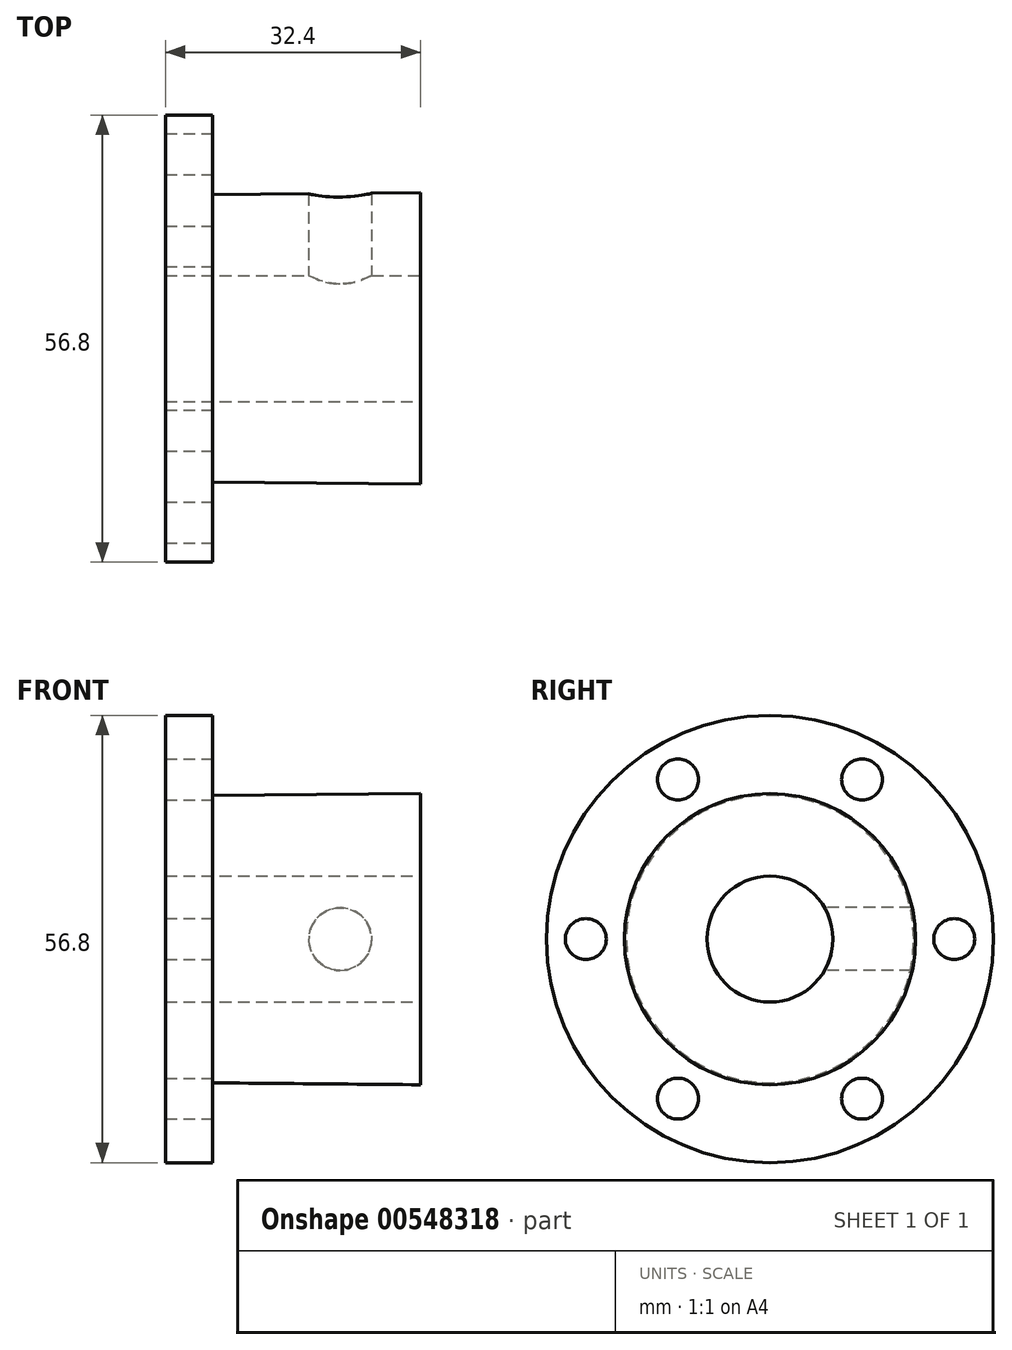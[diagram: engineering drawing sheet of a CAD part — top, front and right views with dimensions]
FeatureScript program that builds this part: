
annotation { "Feature Type Name" : "Feature", "Feature Type Description" : "" }
export const myFeature = defineFeature(function(context is Context, id is Id, definition is map)
    precondition{}
    {
        {
            var Q0;
            Q0=qCreatedBy(makeId("Front.planeOp"),FACE);
            var sketch = newSketch(context, id + "F0", { "sketchPlane" : qUnion([Q0])});
            skLineSegment(sketch, "E0", {"start": v(44.45, 0) * mm, "end": v(0, 0) * mm});
            skLineSegment(sketch, "E1", {"start": v(48.08, 18.5) * mm, "end": v(48.08, 8) * mm});
            skLineSegment(sketch, "E2", {"start": v(48.08, 8) * mm, "end": v(15.68, 8) * mm});
            skLineSegment(sketch, "E3", {"start": v(15.68, 8) * mm, "end": v(15.68, 28.4) * mm});
            skLineSegment(sketch, "E4", {"start": v(15.68, 28.4) * mm, "end": v(21.68, 28.4) * mm});
            skLineSegment(sketch, "E5", {"start": v(21.68, 28.4) * mm, "end": v(21.68, 18.26) * mm});
            skLineSegment(sketch, "E6", {"start": v(21.68, 18.26) * mm, "end": v(48.08, 18.5) * mm});
            skSolve(sketch);
        }
        {
            var Q0;
            Q0=qSketchRegion(id+"F0",true);
            var Q1;
            Q1=sQuery(id+"F0.wireOp",EDGE,"E0");
            revolve(context, id + "F1", {"entities" : qUnion([Q0]), "axis" : qUnion([Q1]), "revolveType" : RevolveType.FULL});
        }
        {
            var Q0;
            Q0=makeQuery(id+"F1.opRevolve","SWEPT_FACE",FACE,{"disambiguationData":[OSD([sQuery(id+"F0.wireOp",EDGE,"E5")])]});
            var sketch = newSketch(context, id + "F2", { "sketchPlane" : qUnion([Q0])});
            skLineSegment(sketch, "E7", {"start": v(0, 0) * mm, "end": v(-46.8, 0) * mm, "construction": true});
            skCircle(sketch, "E8", {"center": v(-23.4, 0) * mm, "radius": 2.6 * mm});
            skCircle(sketch, "E9.1.0", {"center": v(-11.7, -20.26) * mm, "radius": 2.6 * mm});
            skCircle(sketch, "E9.2.0", {"center": v(11.7, -20.26) * mm, "radius": 2.6 * mm});
            skCircle(sketch, "E9.3.0", {"center": v(23.4, 0) * mm, "radius": 2.6 * mm});
            skCircle(sketch, "E9.4.0", {"center": v(11.7, 20.26) * mm, "radius": 2.6 * mm});
            skCircle(sketch, "E9.5.0", {"center": v(-11.7, 20.26) * mm, "radius": 2.6 * mm});
            skPoint(sketch, "E9.center", {"position": v(0, 0) * mm});
            skSolve(sketch);
        }
        {
            var Q0;
            Q0=qSketchRegion(id+"F2",true);
            extrude(context, id + "F3", {"entities" : qUnion([Q0]), "operationType" : NewBodyOperationType.REMOVE, "oppositeDirection" : true, "depth" : 6 * mm, "offsetDistance" : 25 * mm});
        }
        {
            var Q0;
            Q0=qCreatedBy(makeId("Front.planeOp"),FACE);
            var sketch = newSketch(context, id + "F4", { "sketchPlane" : qUnion([Q0])});
            skCircle(sketch, "E10", {"center": v(37.88, 0) * mm, "radius": 4 * mm});
            skSolve(sketch);
        }
        {
            var Q0;
            Q0=qSketchRegion(id+"F4",true);
            var Q1;
            Q1=sQuery(id+"F4.wireOp",EDGE,"E10");
            extrude(context, id + "F5", {"entities" : qUnion([Q0]), "operationType" : NewBodyOperationType.REMOVE, "surfaceEntities" : qUnion([Q1]), "endBound" : BoundingType.THROUGH_ALL, "oppositeDirection" : true, "depth" : 25 * mm, "offsetDistance" : 25 * mm});
        }
    });
